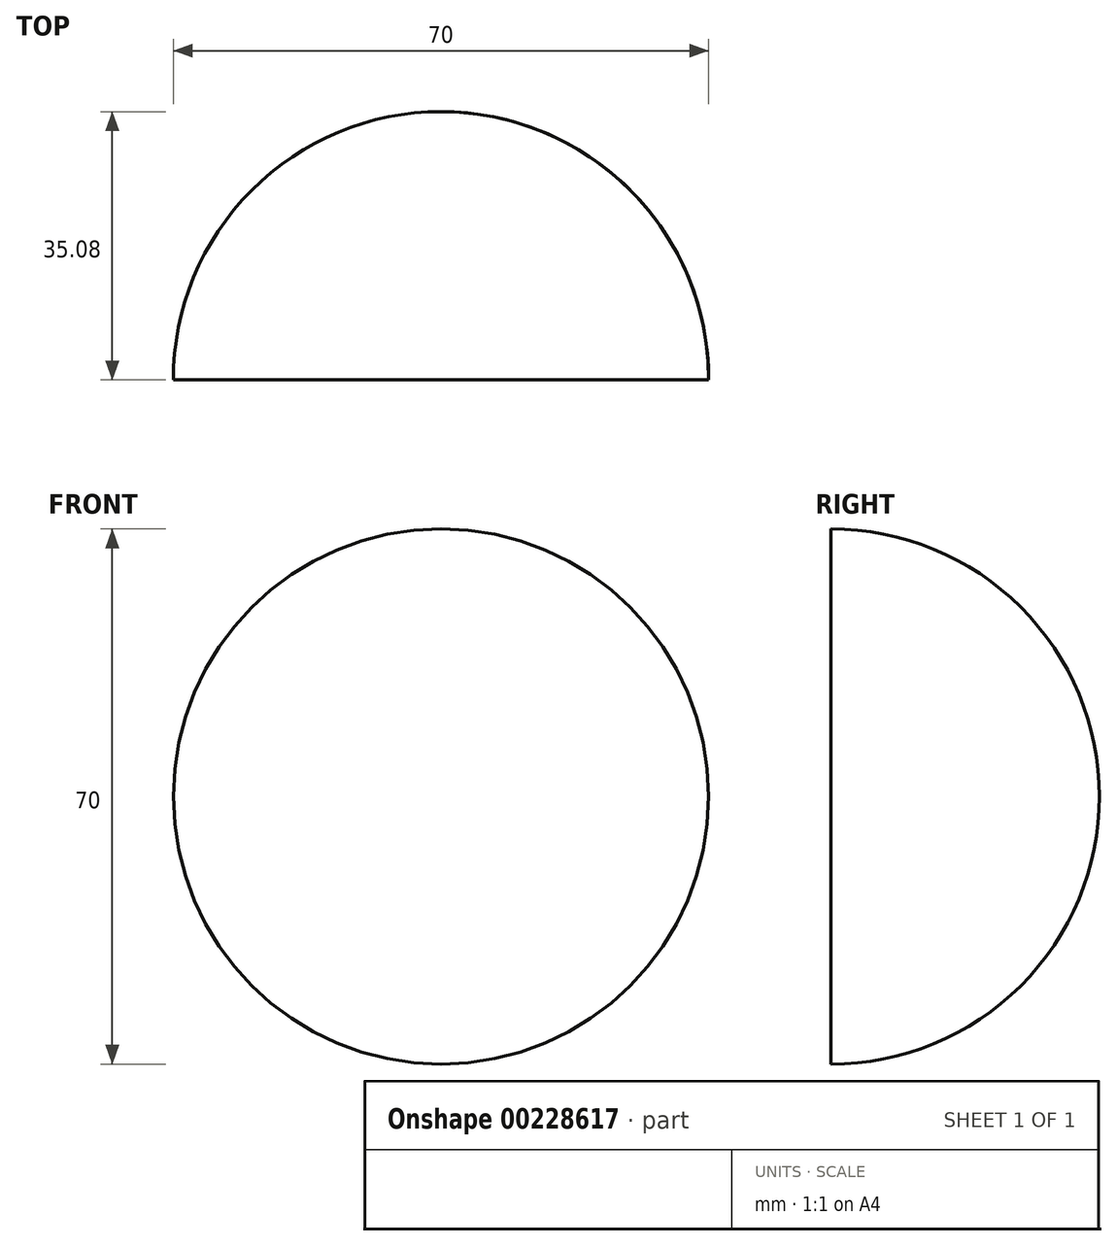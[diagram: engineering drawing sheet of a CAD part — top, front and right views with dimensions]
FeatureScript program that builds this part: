
annotation { "Feature Type Name" : "Feature", "Feature Type Description" : "" }
export const myFeature = defineFeature(function(context is Context, id is Id, definition is map)
    precondition{}
    {
        {
            var Q0;
            Q0=qCreatedBy(makeId("Top.planeOp"),FACE);
            var sketch = newSketch(context, id + "F0", { "sketchPlane" : qUnion([Q0])});
            skArc(sketch, "E0", {"start": v(35, 0) * mm, "mid": v(0, 35.08) * mm, "end": v(-35, 0) * mm});
            skLineSegment(sketch, "E1", {"start": v(0, 35.08) * mm, "end": v(0, 0.08) * mm});
            skLineSegment(sketch, "E2", {"start": v(0, 0) * mm, "end": v(-35, 0) * mm});
            skLineSegment(sketch, "E3", {"start": v(35, 0) * mm, "end": v(0, 0.08) * mm});
            skSolve(sketch);
        }
        {
            var Q0;
            {var subQ2=sQuery(id+"F0.wireOp",EDGE,"E1");Q0=makeQuery(id+"F0.imprint","IMPRINT",FACE,{"disambiguationData":[TD([[makeQuery(id+"F0.imprint","IMPRINT",EDGE,{"derivedFrom":subQ2}),1.0]])]});}
            var Q1;
            Q1=sQuery(id+"F0.wireOp",EDGE,"E1");
            revolve(context, id + "F1", {"surfaceOperationType" : NewSurfaceOperationType.NEW, "entities" : qUnion([Q0]), "axis" : qUnion([Q1]), "revolveType" : RevolveType.FULL});
        }
    });
